# Revit family: super-g_super-g__endteil__hl_led__2_9w_430lm_3000k_cri_80_430-9001_6c1b
name_source: partatom
category: Leuchten
revit_build: Autodesk Revit 2016 (Build: 20190508_0715(x64)
units: mm (PartAtom-declared; Revit-internal decimal feet)

## family parameters
Basisbauteil = Fläche
Beim Laden mit Abzugskörper schneiden = Nein
Bemaßung runder Anschluss = Durchmesser verwenden
Gemeinsam genutzt = Nein
Lichtquelle = Nein
Raumberechnungspunkt = Nein
Teiletyp = Normal

## types (1)
- 430-9001- (1 x LED, 429 lm, 3.2 W, 3000K)
    Approval mark = CE
    Beschreibung = The insert consists of aluminum-extruded profile. Charming SOFT-EDGE design ensure unparalleled styling. Stated photometric values correspond to operation by 0 mA; a suitable ballast needs to be sourced separately and is not scope of delivery. Dimming (# 430-9001) depends on the used ballast and may vary.
    CIE Flux Codes = 47 78 95 100 62
    Color Rendering = 1B/80…89
    Color Temperature = 3000K
    Height = 120 mm
    Hersteller = Prolicht
    Lamp Light Flux = 429 lm
    Lamp Power = 3.2 W
    Lamp count = 1
    Lampe = 1 x LED
    Length = 125 mm
    Luminous efficacy = 84 lm/W
    ModVariant = Nein
    Modell = 430-9001
    Mounting Place = Ceiling
    Mounting Type = Pendant
    Number of Poles = 1
    OnlyDefault = Ja
    Power Factor = 1
    Product Name = SUPER-G__SUPER-G  Endteil  HL LED: 2,9W 430lm 3000K CRI:80
    Product group = Suspended profile systems
    ProductGroupID = 944
    Protection Class = Protection class I
    Protection Degree = IP 20
    RLX_Detail_Level = 1
    RlxData = <blob elided: 47657 chars, md5=3e508a97>
    Scheinlast = 3 VA
    Socket = socket
    Standby Power = 0 W
    System Light Flux = 268 lm
    System Power = 3 W
    Typenbild = 430-9001.jpg
    URL = http://relux.com
    VarID = 430-9001-
    Voltage = 0 V
    Vorgabe-Ansicht = 1800 mm
    Weight = 0.00 kg
    Width = 150 mm

## geometry (parser evidence)
native form markers: Blend x4, Sweep x14
no freeform markers — native parametric forms only
